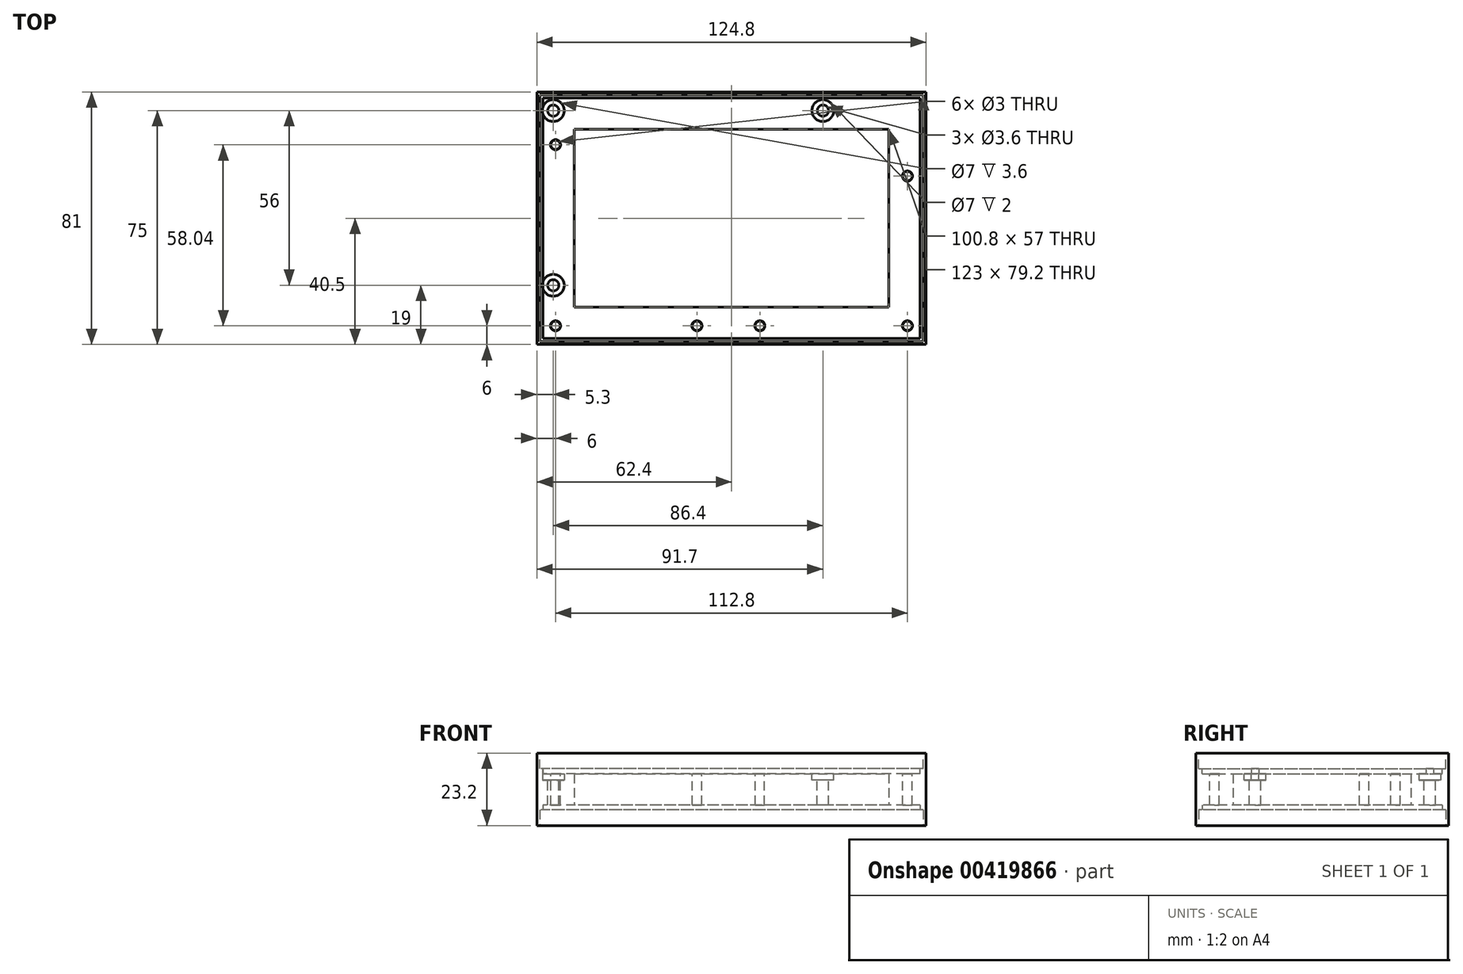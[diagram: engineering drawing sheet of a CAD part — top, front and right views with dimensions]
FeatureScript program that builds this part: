
annotation { "Feature Type Name" : "Feature", "Feature Type Description" : "" }
export const myFeature = defineFeature(function(context is Context, id is Id, definition is map)
    precondition{}
    {
        {
            var Q0;
            Q0=qCreatedBy(makeId("Top.planeOp"),FACE);
            var sketch = newSketch(context, id + "F0", { "sketchPlane" : qUnion([Q0])});
            skLineSegment(sketch, "E0.bottom", {"start": v(62.4, -40.5) * mm, "end": v(-62.4, -40.5) * mm});
            skLineSegment(sketch, "E0.top", {"start": v(62.4, 40.5) * mm, "end": v(-62.4, 40.5) * mm});
            skLineSegment(sketch, "E0.left", {"start": v(62.4, -40.5) * mm, "end": v(62.4, 40.5) * mm});
            skLineSegment(sketch, "E0.right", {"start": v(-62.4, -40.5) * mm, "end": v(-62.4, 40.5) * mm});
            skPoint(sketch, "E0.middle", {"position": v(0, 0) * mm});
            skSolve(sketch);
        }
        {
            var Q0;
            Q0 = qSketchRegion(id + "F0", true);
            extrude(context, id + "F1", {"entities" : qUnion([Q0]), "depth" : 23.2 * mm});
        }
        {
            var Q0;
            Q0=makeQuery(id+"F1.opExtrude","CAP_FACE",FACE,{"disambiguationData":[OSD([sQuery(id+"F0.wireOp",EDGE,"E0.bottom"),sQuery(id+"F0.wireOp",EDGE,"E0.top"),sQuery(id+"F0.wireOp",EDGE,"E0.left"),sQuery(id+"F0.wireOp",EDGE,"E0.right")])],"isStart":false});
            var sketch = newSketch(context, id + "F2", { "sketchPlane" : qUnion([Q0])});
            skLineSegment(sketch, "E1.bottom", {"start": v(61.5, -39.6) * mm, "end": v(-61.5, -39.6) * mm});
            skLineSegment(sketch, "E1.top", {"start": v(61.5, 39.6) * mm, "end": v(-61.5, 39.6) * mm});
            skLineSegment(sketch, "E1.left", {"start": v(61.5, -39.6) * mm, "end": v(61.5, 39.6) * mm});
            skLineSegment(sketch, "E1.right", {"start": v(-61.5, -39.6) * mm, "end": v(-61.5, 39.6) * mm});
            skPoint(sketch, "E1.middle", {"position": v(0, 0) * mm});
            skSolve(sketch);
        }
        {
            var Q0;
            Q0=makeQuery(id+"F2.imprint","IMPRINT",FACE,{"disambiguationData":[TD([[makeQuery(id+"F2.imprint","IMPRINT",EDGE,{"derivedFrom":sQuery(id+"F2.wireOp",EDGE,"E1.bottom")}),-1.0]])]});
            extrude(context, id + "F3", {"entities" : qUnion([Q0]), "operationType" : NewBodyOperationType.REMOVE, "oppositeDirection" : true, "depth" : 5 * mm});
        }
        {
            var Q0;
            Q0=makeQuery(id+"F1.opExtrude","CAP_FACE",FACE,{"disambiguationData":[OSD([sQuery(id+"F0.wireOp",EDGE,"E0.bottom"),sQuery(id+"F0.wireOp",EDGE,"E0.top"),sQuery(id+"F0.wireOp",EDGE,"E0.left"),sQuery(id+"F0.wireOp",EDGE,"E0.right")])],"isStart":true});
            var sketch = newSketch(context, id + "F4", { "sketchPlane" : qUnion([Q0])});
            skLineSegment(sketch, "E2.bottom", {"start": v(61.5, -39.6) * mm, "end": v(-61.5, -39.6) * mm});
            skLineSegment(sketch, "E2.top", {"start": v(61.5, 39.6) * mm, "end": v(-61.5, 39.6) * mm});
            skLineSegment(sketch, "E2.left", {"start": v(61.5, -39.6) * mm, "end": v(61.5, 39.6) * mm});
            skLineSegment(sketch, "E2.right", {"start": v(-61.5, -39.6) * mm, "end": v(-61.5, 39.6) * mm});
            skPoint(sketch, "E2.middle", {"position": v(0, 0) * mm});
            skSolve(sketch);
        }
        {
            var Q0;
            Q0=makeQuery(id+"F4.imprint","IMPRINT",FACE,{"disambiguationData":[TD([[makeQuery(id+"F4.imprint","IMPRINT",EDGE,{"derivedFrom":sQuery(id+"F4.wireOp",EDGE,"E2.bottom")}),-1.0]])]});
            extrude(context, id + "F5", {"entities" : qUnion([Q0]), "operationType" : NewBodyOperationType.REMOVE, "oppositeDirection" : true, "depth" : 5 * mm});
        }
        {
            var Q0;
            Q0=makeQuery(id+"F3.boolean.opBoolean","COPY",FACE,{"derivedFrom":makeQuery(id+"F3.opExtrude","CAP_FACE",FACE,{"disambiguationData":[OSD([sQuery(id+"F2.wireOp",EDGE,"E1.bottom"),sQuery(id+"F2.wireOp",EDGE,"E1.top"),sQuery(id+"F2.wireOp",EDGE,"E1.left"),sQuery(id+"F2.wireOp",EDGE,"E1.right")])],"isStart":false})});
            var sketch = newSketch(context, id + "F6", { "sketchPlane" : qUnion([Q0])});
            skLineSegment(sketch, "E3.bottom", {"start": v(60.4, -38.5) * mm, "end": v(-60.4, -38.5) * mm});
            skLineSegment(sketch, "E3.top", {"start": v(60.4, 38.5) * mm, "end": v(-60.4, 38.5) * mm});
            skLineSegment(sketch, "E3.left", {"start": v(60.4, -38.5) * mm, "end": v(60.4, 38.5) * mm});
            skLineSegment(sketch, "E3.right", {"start": v(-60.4, -38.5) * mm, "end": v(-60.4, 38.5) * mm});
            skPoint(sketch, "E3.middle", {"position": v(0, 0) * mm});
            skSolve(sketch);
        }
        {
            var Q0;
            Q0 = qSketchRegion(id + "F6", true);
            extrude(context, id + "F7", {"entities" : qUnion([Q0]), "operationType" : NewBodyOperationType.REMOVE, "oppositeDirection" : true, "depth" : 1.6 * mm});
        }
        {
            var Q0;
            Q0=makeQuery(id+"F5.boolean.opBoolean","COPY",FACE,{"derivedFrom":makeQuery(id+"F5.opExtrude","CAP_FACE",FACE,{"disambiguationData":[OSD([sQuery(id+"F4.wireOp",EDGE,"E2.bottom"),sQuery(id+"F4.wireOp",EDGE,"E2.top"),sQuery(id+"F4.wireOp",EDGE,"E2.left"),sQuery(id+"F4.wireOp",EDGE,"E2.right")])],"isStart":false})});
            var sketch = newSketch(context, id + "F8", { "sketchPlane" : qUnion([Q0])});
            skLineSegment(sketch, "E4.bottom", {"start": v(60.4, -38.5) * mm, "end": v(-60.4, -38.5) * mm});
            skLineSegment(sketch, "E4.top", {"start": v(60.4, 38.5) * mm, "end": v(-60.4, 38.5) * mm});
            skLineSegment(sketch, "E4.left", {"start": v(60.4, -38.5) * mm, "end": v(60.4, 38.5) * mm});
            skLineSegment(sketch, "E4.right", {"start": v(-60.4, -38.5) * mm, "end": v(-60.4, 38.5) * mm});
            skPoint(sketch, "E4.middle", {"position": v(0, 0) * mm});
            skSolve(sketch);
        }
        {
            var Q0;
            Q0=makeQuery(id+"F8.imprint","IMPRINT",FACE,{"disambiguationData":[TD([[makeQuery(id+"F8.imprint","IMPRINT",EDGE,{"derivedFrom":sQuery(id+"F8.wireOp",EDGE,"E4.bottom")}),-1.0]])]});
            extrude(context, id + "F9", {"entities" : qUnion([Q0]), "operationType" : NewBodyOperationType.REMOVE, "oppositeDirection" : true, "depth" : 1.6 * mm});
        }
        {
            var Q0;
            Q0=makeQuery(id+"F9.boolean.opBoolean","COPY",FACE,{"derivedFrom":makeQuery(id+"F9.opExtrude","CAP_FACE",FACE,{"disambiguationData":[OSD([sQuery(id+"F8.wireOp",EDGE,"E4.bottom"),sQuery(id+"F8.wireOp",EDGE,"E4.top"),sQuery(id+"F8.wireOp",EDGE,"E4.left"),sQuery(id+"F8.wireOp",EDGE,"E4.right")])],"isStart":false})});
            var sketch = newSketch(context, id + "F10", { "sketchPlane" : qUnion([Q0])});
            skLineSegment(sketch, "E5.bottom", {"start": v(50.4, -28.5) * mm, "end": v(-50.4, -28.5) * mm});
            skLineSegment(sketch, "E5.top", {"start": v(50.4, 28.5) * mm, "end": v(-50.4, 28.5) * mm});
            skLineSegment(sketch, "E5.left", {"start": v(50.4, -28.5) * mm, "end": v(50.4, 28.5) * mm});
            skLineSegment(sketch, "E5.right", {"start": v(-50.4, -28.5) * mm, "end": v(-50.4, 28.5) * mm});
            skPoint(sketch, "E5.middle", {"position": v(0, 0) * mm});
            skSolve(sketch);
        }
        {
            var Q0;
            Q0=makeQuery(id+"F10.imprint","IMPRINT",FACE,{"disambiguationData":[TD([[makeQuery(id+"F10.imprint","IMPRINT",EDGE,{"derivedFrom":sQuery(id+"F10.wireOp",EDGE,"E5.bottom")}),-1.0]])]});
            extrude(context, id + "F11", {"entities" : qUnion([Q0]), "operationType" : NewBodyOperationType.REMOVE, "endBound" : BoundingType.THROUGH_ALL, "oppositeDirection" : true, "depth" : 25 * mm});
        }
        {
            var Q0;
            Q0=makeQuery(id+"F7.boolean.opBoolean","COPY",FACE,{"derivedFrom":makeQuery(id+"F7.opExtrude","CAP_FACE",FACE,{"disambiguationData":[OSD([sQuery(id+"F6.wireOp",EDGE,"E3.bottom"),sQuery(id+"F6.wireOp",EDGE,"E3.top"),sQuery(id+"F6.wireOp",EDGE,"E3.left"),sQuery(id+"F6.wireOp",EDGE,"E3.right")])],"isStart":false})});
            var sketch = newSketch(context, id + "F12", { "sketchPlane" : qUnion([Q0])});
            skCircle(sketch, "E6", {"center": v(-57.1, 34.5) * mm, "radius": 1.8 * mm});
            skSolve(sketch);
        }
        {
            var Q0;
            Q0=makeQuery(id+"F12.imprint","IMPRINT",FACE,{"disambiguationData":[TD([[makeQuery(id+"F12.imprint","IMPRINT",EDGE,{"derivedFrom":sQuery(id+"F12.wireOp",EDGE,"E6")}),-1.0]])]});
            var sketch = newSketch(context, id + "F13", { "sketchPlane" : qUnion([Q0])});
            skCircle(sketch, "E7", {"center": v(-57.1, 34.5) * mm, "radius": 3.5 * mm});
            skSolve(sketch);
        }
        {
            var Q0;
            Q0 = qSketchRegion(id + "F13", true);
            extrude(context, id + "F14", {"entities" : qUnion([Q0]), "operationType" : NewBodyOperationType.REMOVE, "endBound" : BoundingType.THROUGH_ALL, "depth" : 25 * mm});
        }
        {
            var Q0;
            Q0 = qSketchRegion(id + "F13", true);
            extrude(context, id + "F15", {"entities" : qUnion([Q0]), "operationType" : NewBodyOperationType.REMOVE, "oppositeDirection" : true, "depth" : 2 * mm});
        }
        {
            var Q0;
            Q0 = qSketchRegion(id + "F12", true);
            extrude(context, id + "F16", {"entities" : qUnion([Q0]), "operationType" : NewBodyOperationType.REMOVE, "endBound" : BoundingType.THROUGH_ALL, "oppositeDirection" : true, "depth" : 25 * mm});
        }
        {
            var Q0;
            Q0=makeQuery(id+"F14.boolean.opBoolean","MERGE",FACE,{"derivedFrom":[makeQuery(id+"F7.boolean.opBoolean","COPY",FACE,{"derivedFrom":makeQuery(id+"F7.opExtrude","CAP_FACE",FACE,{"disambiguationData":[OSD([sQuery(id+"F6.wireOp",EDGE,"E3.bottom"),sQuery(id+"F6.wireOp",EDGE,"E3.top"),sQuery(id+"F6.wireOp",EDGE,"E3.left"),sQuery(id+"F6.wireOp",EDGE,"E3.right")])],"isStart":false})}),makeQuery(id+"F14.opExtrude","CAP_FACE",FACE,{"disambiguationData":[OSD([sQuery(id+"F13.wireOp",EDGE,"E7")])],"isStart":true})]});
            var sketch = newSketch(context, id + "F17", { "sketchPlane" : qUnion([Q0])});
            skCircle(sketch, "E8", {"center": v(29.3, 34.5) * mm, "radius": 1.8 * mm});
            skSolve(sketch);
        }
        {
            var Q0;
            Q0=makeQuery(id+"F17.imprint","IMPRINT",FACE,{"disambiguationData":[TD([[makeQuery(id+"F17.imprint","IMPRINT",EDGE,{"derivedFrom":sQuery(id+"F17.wireOp",EDGE,"E8")}),-1.0]])]});
            var sketch = newSketch(context, id + "F18", { "sketchPlane" : qUnion([Q0])});
            skCircle(sketch, "E9", {"center": v(29.3, 34.5) * mm, "radius": 3.5 * mm});
            skSolve(sketch);
        }
        {
            var Q0;
            Q0 = qSketchRegion(id + "F17", true);
            extrude(context, id + "F19", {"entities" : qUnion([Q0]), "operationType" : NewBodyOperationType.REMOVE, "endBound" : BoundingType.THROUGH_ALL, "oppositeDirection" : true, "depth" : 25 * mm});
        }
        {
            var Q0;
            Q0 = qSketchRegion(id + "F18", true);
            extrude(context, id + "F20", {"entities" : qUnion([Q0]), "operationType" : NewBodyOperationType.REMOVE, "oppositeDirection" : true, "depth" : 2 * mm});
        }
        {
            var Q0;
            Q0=makeQuery(id+"F14.boolean.opBoolean","MERGE",FACE,{"derivedFrom":[makeQuery(id+"F7.boolean.opBoolean","COPY",FACE,{"derivedFrom":makeQuery(id+"F7.opExtrude","CAP_FACE",FACE,{"disambiguationData":[OSD([sQuery(id+"F6.wireOp",EDGE,"E3.bottom"),sQuery(id+"F6.wireOp",EDGE,"E3.top"),sQuery(id+"F6.wireOp",EDGE,"E3.left"),sQuery(id+"F6.wireOp",EDGE,"E3.right")])],"isStart":false})}),makeQuery(id+"F14.opExtrude","CAP_FACE",FACE,{"disambiguationData":[OSD([sQuery(id+"F13.wireOp",EDGE,"E7")])],"isStart":true})]});
            var sketch = newSketch(context, id + "F21", { "sketchPlane" : qUnion([Q0])});
            skCircle(sketch, "E10", {"center": v(-57.1, -21.5) * mm, "radius": 1.8 * mm});
            skSolve(sketch);
        }
        {
            var Q0;
            Q0=makeQuery(id+"F21.imprint","IMPRINT",FACE,{"disambiguationData":[TD([[makeQuery(id+"F21.imprint","IMPRINT",EDGE,{"derivedFrom":sQuery(id+"F21.wireOp",EDGE,"E10")}),-1.0]])]});
            var sketch = newSketch(context, id + "F22", { "sketchPlane" : qUnion([Q0])});
            skCircle(sketch, "E11", {"center": v(-57.1, -21.5) * mm, "radius": 3.5 * mm});
            skSolve(sketch);
        }
        {
            var Q0;
            Q0 = qSketchRegion(id + "F21", true);
            extrude(context, id + "F23", {"entities" : qUnion([Q0]), "operationType" : NewBodyOperationType.REMOVE, "endBound" : BoundingType.THROUGH_ALL, "oppositeDirection" : true, "depth" : 25 * mm});
        }
        {
            var Q0;
            Q0=makeQuery(id+"F22.imprint","IMPRINT",FACE,{"disambiguationData":[TD([[makeQuery(id+"F22.imprint","IMPRINT",EDGE,{"derivedFrom":makeQuery(id+"F21.imprint","IMPRINT",EDGE,{"derivedFrom":sQuery(id+"F21.wireOp",EDGE,"E10")})}),-1.0]])]});
            var Q1;
            Q1=sQuery(id+"F22.wireOp",EDGE,"E11");
            extrude(context, id + "F24", {"entities" : qUnion([Q0]), "operationType" : NewBodyOperationType.REMOVE, "surfaceEntities" : qUnion([Q1]), "oppositeDirection" : true, "depth" : 2 * mm});
        }
        {
            var Q0;
            Q0 = qSketchRegion(id + "F22", true);
            extrude(context, id + "F25", {"entities" : qUnion([Q0]), "operationType" : NewBodyOperationType.REMOVE, "depth" : 25 * mm});
        }
        {
            var Q0;
            Q0=makeQuery(id+"F14.boolean.opBoolean","MERGE",FACE,{"derivedFrom":[makeQuery(id+"F7.boolean.opBoolean","COPY",FACE,{"derivedFrom":makeQuery(id+"F7.opExtrude","CAP_FACE",FACE,{"disambiguationData":[OSD([sQuery(id+"F6.wireOp",EDGE,"E3.bottom"),sQuery(id+"F6.wireOp",EDGE,"E3.top"),sQuery(id+"F6.wireOp",EDGE,"E3.left"),sQuery(id+"F6.wireOp",EDGE,"E3.right")])],"isStart":false})}),makeQuery(id+"F14.opExtrude","CAP_FACE",FACE,{"disambiguationData":[OSD([sQuery(id+"F13.wireOp",EDGE,"E7")])],"isStart":true})]});
            var sketch = newSketch(context, id + "F26", { "sketchPlane" : qUnion([Q0])});
            skPoint(sketch, "E12", {"position": v(-56.4, -34.5) * mm});
            skPoint(sketch, "E13", {"position": v(56.4, -34.5) * mm});
            skPoint(sketch, "E14", {"position": v(-11.06, -34.5) * mm});
            skPoint(sketch, "E15", {"position": v(9.1, -34.5) * mm});
            skPoint(sketch, "E16", {"position": v(56.4, 13.5) * mm});
            skPoint(sketch, "E17", {"position": v(-56.4, 23.54) * mm});
            skSolve(sketch);
        }
        {
            var Q0;
            Q0=sQuery(id+"F26.wireOp",VERTEX,"E16");
            var Q1;
            Q1=sQuery(id+"F26.wireOp",VERTEX,"E13");
            var Q2;
            Q2=sQuery(id+"F26.wireOp",VERTEX,"E15");
            var Q3;
            Q3=sQuery(id+"F26.wireOp",VERTEX,"E14");
            var Q4;
            Q4=sQuery(id+"F26.wireOp",VERTEX,"E12");
            var Q5;
            Q5=sQuery(id+"F26.wireOp",VERTEX,"E17");
            var Q6;
            Q6=makeQuery(id+"F1.opExtrude","SWEPT_BODY",BODY,{"disambiguationData":[OSD([sQuery(id+"F0.wireOp",EDGE,"E0.bottom"),sQuery(id+"F0.wireOp",EDGE,"E0.top"),sQuery(id+"F0.wireOp",EDGE,"E0.left"),sQuery(id+"F0.wireOp",EDGE,"E0.right")])]});
            hole(context, id + "F27", {"style" : HoleStyle.C_SINK, "endStyle" : HoleEndStyle.THROUGH, "holeDiameter" : 3 * mm, "cSinkDiameter" : 3.28 * mm, "cSinkAngle" : 90 * degree, "isTappedThrough" : true, "tappedDepth" : 12 * mm, "tapClearance" : 3, "locations" : qUnion([Q0, Q1, Q2, Q3, Q4, Q5]), "scope" : qUnion([Q6])});
        }
    });
